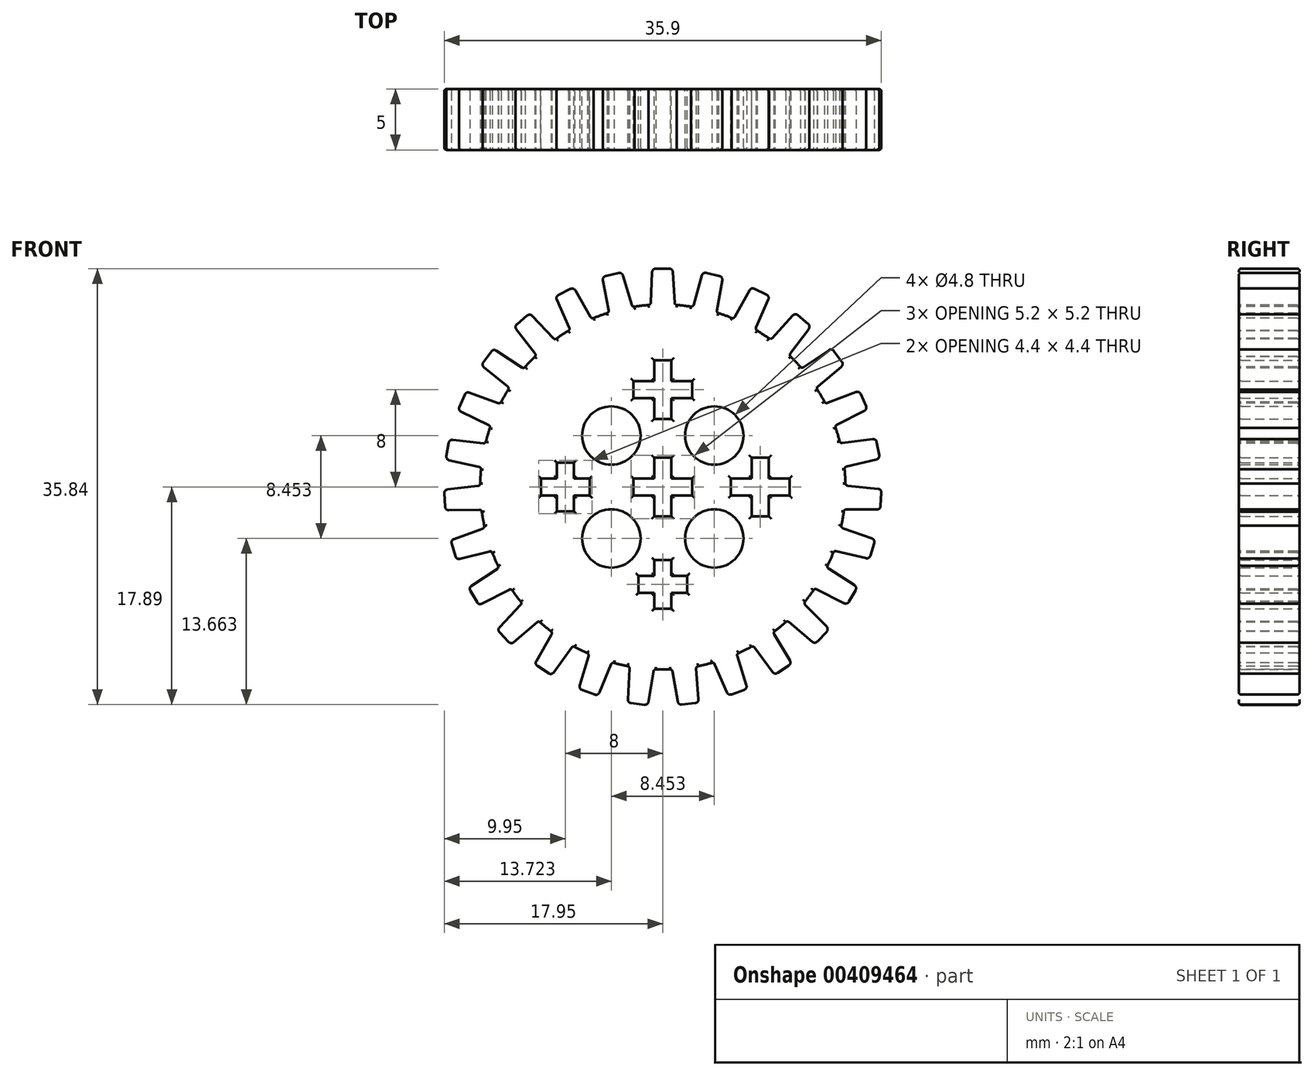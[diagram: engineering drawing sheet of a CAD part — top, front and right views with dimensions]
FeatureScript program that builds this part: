
annotation { "Feature Type Name" : "Feature", "Feature Type Description" : "" }
export const myFeature = defineFeature(function(context is Context, id is Id, definition is map)
    precondition{}
    {
        {
            var Q0;
            Q0=qCreatedBy(makeId("Front.planeOp"),FACE);
            var sketch = newSketch(context, id + "F0", { "sketchPlane" : qUnion([Q0])});
            skCircle(sketch, "E0", {"center": v(0, 0) * mm, "radius": 15 * mm});
            skLineSegment(sketch, "E1.bottom", {"start": v(0.7, -2.4) * mm, "end": v(-0.7, -2.4) * mm});
            skLineSegment(sketch, "E1.top", {"start": v(0.7, 2.4) * mm, "end": v(-0.7, 2.4) * mm});
            skLineSegment(sketch, "E1.left", {"start": v(0.7, -2.4) * mm, "end": v(0.7, 2.4) * mm});
            skLineSegment(sketch, "E1.right", {"start": v(-0.7, -2.4) * mm, "end": v(-0.7, 2.4) * mm});
            skLineSegment(sketch, "E2.bottom", {"start": v(2.4, -0.7) * mm, "end": v(-2.4, -0.7) * mm});
            skLineSegment(sketch, "E2.top", {"start": v(2.4, 0.7) * mm, "end": v(-2.4, 0.7) * mm});
            skLineSegment(sketch, "E2.left", {"start": v(2.4, -0.7) * mm, "end": v(2.4, 0.7) * mm});
            skLineSegment(sketch, "E2.right", {"start": v(-2.4, -0.7) * mm, "end": v(-2.4, 0.7) * mm});
            skLineSegment(sketch, "E3", {"start": v(-21.58, 0) * mm, "end": v(19.66, 0) * mm, "construction": true});
            skPoint(sketch, "E3.startSnap0", {"position": v(-2.4, 0) * mm});
            skPoint(sketch, "E3.endSnap0", {"position": v(-2.4, 0) * mm});
            skLineSegment(sketch, "E4", {"start": v(0, -18.97) * mm, "end": v(0, 17.04) * mm, "construction": true});
            skPoint(sketch, "E4.startSnap0", {"position": v(0, -2.4) * mm});
            skLineSegment(sketch, "E5.bottom", {"start": v(0.7, 5.6) * mm, "end": v(-0.7, 5.6) * mm});
            skLineSegment(sketch, "E5.top", {"start": v(0.7, 10.4) * mm, "end": v(-0.7, 10.4) * mm});
            skLineSegment(sketch, "E5.left", {"start": v(0.7, 5.6) * mm, "end": v(0.7, 10.4) * mm});
            skLineSegment(sketch, "E5.right", {"start": v(-0.7, 5.6) * mm, "end": v(-0.7, 10.4) * mm});
            skPoint(sketch, "E5.middle", {"position": v(0, 8) * mm});
            skLineSegment(sketch, "E6.bottom", {"start": v(2.4, 7.3) * mm, "end": v(-2.4, 7.3) * mm});
            skLineSegment(sketch, "E6.top", {"start": v(2.4, 8.7) * mm, "end": v(-2.4, 8.7) * mm});
            skLineSegment(sketch, "E6.left", {"start": v(2.4, 7.3) * mm, "end": v(2.4, 8.7) * mm});
            skLineSegment(sketch, "E6.right", {"start": v(-2.4, 7.3) * mm, "end": v(-2.4, 8.7) * mm});
            skLineSegment(sketch, "E7.bottom", {"start": v(0.7, -10) * mm, "end": v(-0.7, -10) * mm});
            skLineSegment(sketch, "E7.top", {"start": v(0.7, -6) * mm, "end": v(-0.7, -6) * mm});
            skLineSegment(sketch, "E7.left", {"start": v(0.7, -10) * mm, "end": v(0.7, -6) * mm});
            skLineSegment(sketch, "E7.right", {"start": v(-0.7, -10) * mm, "end": v(-0.7, -6) * mm});
            skPoint(sketch, "E7.middle", {"position": v(0, -8) * mm});
            skLineSegment(sketch, "E8.bottom", {"start": v(2, -8.7) * mm, "end": v(-2, -8.7) * mm});
            skLineSegment(sketch, "E8.top", {"start": v(2, -7.3) * mm, "end": v(-2, -7.3) * mm});
            skLineSegment(sketch, "E8.left", {"start": v(2, -8.7) * mm, "end": v(2, -7.3) * mm});
            skLineSegment(sketch, "E8.right", {"start": v(-2, -8.7) * mm, "end": v(-2, -7.3) * mm});
            skLineSegment(sketch, "E9.1.0", {"start": v(8.7, -2.4) * mm, "end": v(8.7, 2.4) * mm});
            skPoint(sketch, "E9.1.1", {"position": v(8, 0) * mm});
            skLineSegment(sketch, "E9.1.2", {"start": v(7.3, 2.4) * mm, "end": v(8.7, 2.4) * mm});
            skLineSegment(sketch, "E9.1.3", {"start": v(-18.97, 0) * mm, "end": v(17.04, 0) * mm, "construction": true});
            skLineSegment(sketch, "E9.1.4", {"start": v(5.6, -0.7) * mm, "end": v(10.4, -0.7) * mm});
            skLineSegment(sketch, "E9.1.5", {"start": v(5.6, 0.7) * mm, "end": v(10.4, 0.7) * mm});
            skLineSegment(sketch, "E9.1.6", {"start": v(7.3, -2.4) * mm, "end": v(7.3, 2.4) * mm});
            skLineSegment(sketch, "E9.1.7", {"start": v(7.3, -2.4) * mm, "end": v(8.7, -2.4) * mm});
            skLineSegment(sketch, "E9.1.8", {"start": v(5.6, -0.7) * mm, "end": v(5.6, 0.7) * mm});
            skPoint(sketch, "E9.1.9", {"position": v(8, 0) * mm});
            skLineSegment(sketch, "E9.1.10", {"start": v(10.4, -0.7) * mm, "end": v(10.4, 0.7) * mm});
            skLineSegment(sketch, "E9.1.11", {"start": v(-8.7, -2) * mm, "end": v(-8.7, 2) * mm});
            skLineSegment(sketch, "E9.1.12", {"start": v(-10, 0.7) * mm, "end": v(-6, 0.7) * mm});
            skLineSegment(sketch, "E9.1.13", {"start": v(-8.7, 2) * mm, "end": v(-7.3, 2) * mm});
            skLineSegment(sketch, "E9.1.14", {"start": v(-8.7, -2) * mm, "end": v(-7.3, -2) * mm});
            skPoint(sketch, "E9.1.15", {"position": v(-8, 0) * mm});
            skLineSegment(sketch, "E9.1.16", {"start": v(-10, -0.7) * mm, "end": v(-6, -0.7) * mm});
            skLineSegment(sketch, "E9.1.17", {"start": v(-7.3, -2) * mm, "end": v(-7.3, 2) * mm});
            skPoint(sketch, "E9.1.18", {"position": v(-8, 0) * mm});
            skLineSegment(sketch, "E9.1.19", {"start": v(-6, -0.7) * mm, "end": v(-6, 0.7) * mm});
            skLineSegment(sketch, "E9.1.20", {"start": v(-10, -0.7) * mm, "end": v(-10, 0.7) * mm});
            skLineSegment(sketch, "E9.anchor1", {"start": v(0, 0) * mm, "end": v(0, -18.97) * mm, "construction": true});
            skLineSegment(sketch, "E9.anchor2", {"start": v(0, 0) * mm, "end": v(-18.97, 0) * mm, "construction": true});
            skLineSegment(sketch, "E10", {"start": v(0, 0) * mm, "end": v(8.45, 8.45) * mm, "construction": true});
            skCircle(sketch, "E11", {"center": v(4.23, 4.23) * mm, "radius": 2.4 * mm});
            skCircle(sketch, "E12.1.0", {"center": v(4.23, -4.23) * mm, "radius": 2.4 * mm});
            skCircle(sketch, "E12.2.0", {"center": v(-4.23, -4.23) * mm, "radius": 2.4 * mm});
            skCircle(sketch, "E12.3.0", {"center": v(-4.23, 4.23) * mm, "radius": 2.4 * mm});
            skLineSegment(sketch, "E12.anchor1", {"start": v(0, 0) * mm, "end": v(4.23, 4.23) * mm, "construction": true});
            skLineSegment(sketch, "E12.anchor2", {"start": v(0, 0) * mm, "end": v(-4.23, 4.23) * mm, "construction": true});
            skSolve(sketch);
        }
        {
            var Q0;
            Q0=makeQuery(id+"F0.imprint","IMPRINT",FACE,{"disambiguationData":[TD([[makeQuery(id+"F0.imprint","IMPRINT",EDGE,{"derivedFrom":sQuery(id+"F0.wireOp",EDGE,"E0")}),1.0]])]});
            extrude(context, id + "F1", {"entities" : qUnion([Q0]), "depth" : 5 * mm});
        }
        {
            var Q0;
            Q0=makeQuery(id+"F1.opExtrude","CAP_FACE",FACE,{"disambiguationData":[OSD([sQuery(id+"F0.wireOp",EDGE,"E0"),sQuery(id+"F0.wireOp",EDGE,"E1.bottom"),sQuery(id+"F0.wireOp",EDGE,"E1.top"),sQuery(id+"F0.wireOp",EDGE,"E1.left"),sQuery(id+"F0.wireOp",EDGE,"E1.right"),sQuery(id+"F0.wireOp",EDGE,"E2.bottom"),sQuery(id+"F0.wireOp",EDGE,"E2.top"),sQuery(id+"F0.wireOp",EDGE,"E2.left"),sQuery(id+"F0.wireOp",EDGE,"E2.right")])],"isStart":false});
            var sketch = newSketch(context, id + "F2", { "sketchPlane" : qUnion([Q0])});
            skLineSegment(sketch, "E13.bottom", {"start": v(-0.58, 17.95) * mm, "end": v(0.52, 17.95) * mm});
            skLineSegment(sketch, "E13.left", {"start": v(-0.88, 17.66) * mm, "end": v(-1, 15.14) * mm});
            skLineSegment(sketch, "E13.right", {"start": v(0.82, 17.66) * mm, "end": v(0.97, 15.14) * mm});
            skPoint(sketch, "E14.visualSharp", {"position": v(-0.87, 17.95) * mm});
            skArc(sketch, "E14.filletArc", {"start": v(-0.58, 17.95) * mm, "mid": v(-0.79, 17.86) * mm, "end": v(-0.88, 17.66) * mm});
            skPoint(sketch, "E15.visualSharp", {"position": v(0.8, 17.95) * mm});
            skArc(sketch, "E15.filletArc", {"start": v(0.82, 17.66) * mm, "mid": v(0.73, 17.86) * mm, "end": v(0.52, 17.95) * mm});
            skLineSegment(sketch, "E16", {"start": v(0, -26.44) * mm, "end": v(0, 27.35) * mm, "construction": true});
            skPoint(sketch, "E17.visualSharp", {"position": v(-1, 14.93) * mm});
            skArc(sketch, "E17.filletArc", {"start": v(-1.17, 14.95) * mm, "mid": v(-1.05, 15.02) * mm, "end": v(-1, 15.14) * mm});
            skPoint(sketch, "E18.visualSharp", {"position": v(0.98, 14.94) * mm});
            skArc(sketch, "E18.filletArc", {"start": v(0.97, 15.14) * mm, "mid": v(1.02, 15.02) * mm, "end": v(1.15, 14.96) * mm});
            skSolve(sketch);
        }
        {
            var Q0;
            Q0=makeQuery(id+"F2.imprint","IMPRINT",FACE,{"disambiguationData":[TD([[makeQuery(id+"F2.imprint","IMPRINT",EDGE,{"derivedFrom":sQuery(id+"F2.wireOp",EDGE,"E13.bottom")}),-1.0]])]});
            var Q1;
            Q1=makeQuery(id+"F1.opExtrude","CAP_FACE",FACE,{"disambiguationData":[OSD([sQuery(id+"F0.wireOp",EDGE,"E0"),sQuery(id+"F0.wireOp",EDGE,"E1.bottom"),sQuery(id+"F0.wireOp",EDGE,"E1.top"),sQuery(id+"F0.wireOp",EDGE,"E1.left"),sQuery(id+"F0.wireOp",EDGE,"E1.right"),sQuery(id+"F0.wireOp",EDGE,"E2.bottom"),sQuery(id+"F0.wireOp",EDGE,"E2.top"),sQuery(id+"F0.wireOp",EDGE,"E2.left"),sQuery(id+"F0.wireOp",EDGE,"E2.right"),sQuery(id+"F0.wireOp",EDGE,"E5.bottom"),sQuery(id+"F0.wireOp",EDGE,"E5.top"),sQuery(id+"F0.wireOp",EDGE,"E5.left"),sQuery(id+"F0.wireOp",EDGE,"E5.right"),sQuery(id+"F0.wireOp",EDGE,"E6.bottom"),sQuery(id+"F0.wireOp",EDGE,"E6.top"),sQuery(id+"F0.wireOp",EDGE,"E6.left"),sQuery(id+"F0.wireOp",EDGE,"E6.right"),sQuery(id+"F0.wireOp",EDGE,"E7.bottom"),sQuery(id+"F0.wireOp",EDGE,"E7.top"),sQuery(id+"F0.wireOp",EDGE,"E7.left"),sQuery(id+"F0.wireOp",EDGE,"E7.right"),sQuery(id+"F0.wireOp",EDGE,"E8.bottom"),sQuery(id+"F0.wireOp",EDGE,"E8.top"),sQuery(id+"F0.wireOp",EDGE,"E8.left"),sQuery(id+"F0.wireOp",EDGE,"E8.right"),sQuery(id+"F0.wireOp",EDGE,"E9.1.0"),sQuery(id+"F0.wireOp",EDGE,"E9.1.2"),sQuery(id+"F0.wireOp",EDGE,"E9.1.4"),sQuery(id+"F0.wireOp",EDGE,"E9.1.5"),sQuery(id+"F0.wireOp",EDGE,"E9.1.6"),sQuery(id+"F0.wireOp",EDGE,"E9.1.7"),sQuery(id+"F0.wireOp",EDGE,"E9.1.8"),sQuery(id+"F0.wireOp",EDGE,"E9.1.10"),sQuery(id+"F0.wireOp",EDGE,"E9.1.11"),sQuery(id+"F0.wireOp",EDGE,"E9.1.12"),sQuery(id+"F0.wireOp",EDGE,"E9.1.13"),sQuery(id+"F0.wireOp",EDGE,"E9.1.14"),sQuery(id+"F0.wireOp",EDGE,"E9.1.16"),sQuery(id+"F0.wireOp",EDGE,"E9.1.17"),sQuery(id+"F0.wireOp",EDGE,"E9.1.19"),sQuery(id+"F0.wireOp",EDGE,"E9.1.20"),sQuery(id+"F0.wireOp",EDGE,"E11"),sQuery(id+"F0.wireOp",EDGE,"E12.1.0"),sQuery(id+"F0.wireOp",EDGE,"E12.2.0"),sQuery(id+"F0.wireOp",EDGE,"E12.3.0")])],"isStart":true});
            extrude(context, id + "F3", {"entities" : qUnion([Q0]), "flatOperationType" : FlatOperationType.REMOVE, "endBound" : BoundingType.UP_TO_SURFACE, "oppositeDirection" : true, "endBoundEntityFace" : qUnion([Q1]), "offsetDistance" : 25 * mm, "depth" : 25 * mm, "domain" : OperationDomain.MODEL});
        }
        {
            var Q0;
            Q0=makeQuery(id+"F3.opExtrude","SWEPT_BODY",BODY,{"disambiguationData":[OSD([sQuery(id+"F0.wireOp",EDGE,"E0"),sQuery(id+"F2.wireOp",EDGE,"E13.bottom"),sQuery(id+"F2.wireOp",EDGE,"E13.left"),sQuery(id+"F2.wireOp",EDGE,"E13.right"),sQuery(id+"F2.wireOp",EDGE,"E14.filletArc"),sQuery(id+"F2.wireOp",EDGE,"E15.filletArc")])]});
            var Q1;
            Q1=makeQuery(id+"F1.opExtrude","CAP_EDGE",EDGE,{"disambiguationData":[OSD([sQuery(id+"F0.wireOp",EDGE,"E0")])],"isStart":false});
            circularPattern(context, id + "F4", {"operationType" : NewBodyOperationType.ADD, "entities" : qUnion([Q0]), "axis" : qUnion([Q1]), "angle" : 360 * degree, "instanceCount" : 27, "equalSpace" : true});
        }
        {
            var Q0;
            {var subQ0=sQuery(id+"F0.wireOp",EDGE,"E0");var subQ1=makeQuery(id+"F3.opExtrude","CAP_FACE",FACE,{"disambiguationData":[OSD([subQ0,sQuery(id+"F2.wireOp",EDGE,"E13.bottom"),sQuery(id+"F2.wireOp",EDGE,"E13.left"),sQuery(id+"F2.wireOp",EDGE,"E13.right"),sQuery(id+"F2.wireOp",EDGE,"E14.filletArc"),sQuery(id+"F2.wireOp",EDGE,"E15.filletArc")])],"isStart":true});Q0=makeQuery(id+"F4.boolean.opBoolean","MERGE",FACE,{"derivedFrom":[makeQuery(id+"F1.opExtrude","CAP_FACE",FACE,{"disambiguationData":[OSD([subQ0,sQuery(id+"F0.wireOp",EDGE,"E1.bottom"),sQuery(id+"F0.wireOp",EDGE,"E1.top"),sQuery(id+"F0.wireOp",EDGE,"E1.left"),sQuery(id+"F0.wireOp",EDGE,"E1.right"),sQuery(id+"F0.wireOp",EDGE,"E2.bottom"),sQuery(id+"F0.wireOp",EDGE,"E2.top"),sQuery(id+"F0.wireOp",EDGE,"E2.left"),sQuery(id+"F0.wireOp",EDGE,"E2.right"),sQuery(id+"F0.wireOp",EDGE,"E5.bottom"),sQuery(id+"F0.wireOp",EDGE,"E5.top"),sQuery(id+"F0.wireOp",EDGE,"E5.left"),sQuery(id+"F0.wireOp",EDGE,"E5.right"),sQuery(id+"F0.wireOp",EDGE,"E6.bottom"),sQuery(id+"F0.wireOp",EDGE,"E6.top"),sQuery(id+"F0.wireOp",EDGE,"E6.left"),sQuery(id+"F0.wireOp",EDGE,"E6.right"),sQuery(id+"F0.wireOp",EDGE,"E7.bottom"),sQuery(id+"F0.wireOp",EDGE,"E7.top"),sQuery(id+"F0.wireOp",EDGE,"E7.left"),sQuery(id+"F0.wireOp",EDGE,"E7.right"),sQuery(id+"F0.wireOp",EDGE,"E8.bottom"),sQuery(id+"F0.wireOp",EDGE,"E8.top"),sQuery(id+"F0.wireOp",EDGE,"E8.left"),sQuery(id+"F0.wireOp",EDGE,"E8.right"),sQuery(id+"F0.wireOp",EDGE,"E9.1.0"),sQuery(id+"F0.wireOp",EDGE,"E9.1.2"),sQuery(id+"F0.wireOp",EDGE,"E9.1.4"),sQuery(id+"F0.wireOp",EDGE,"E9.1.5"),sQuery(id+"F0.wireOp",EDGE,"E9.1.6"),sQuery(id+"F0.wireOp",EDGE,"E9.1.7"),sQuery(id+"F0.wireOp",EDGE,"E9.1.8"),sQuery(id+"F0.wireOp",EDGE,"E9.1.10"),sQuery(id+"F0.wireOp",EDGE,"E9.1.11"),sQuery(id+"F0.wireOp",EDGE,"E9.1.12"),sQuery(id+"F0.wireOp",EDGE,"E9.1.13"),sQuery(id+"F0.wireOp",EDGE,"E9.1.14"),sQuery(id+"F0.wireOp",EDGE,"E9.1.16"),sQuery(id+"F0.wireOp",EDGE,"E9.1.17"),sQuery(id+"F0.wireOp",EDGE,"E9.1.19"),sQuery(id+"F0.wireOp",EDGE,"E9.1.20"),sQuery(id+"F0.wireOp",EDGE,"E11"),sQuery(id+"F0.wireOp",EDGE,"E12.1.0"),sQuery(id+"F0.wireOp",EDGE,"E12.2.0"),sQuery(id+"F0.wireOp",EDGE,"E12.3.0")])],"isStart":false}),subQ1,makeQuery(id+"F4.opPattern","COPY",FACE,{"derivedFrom":subQ1,"instanceName":"1"}),makeQuery(id+"F4.opPattern","COPY",FACE,{"derivedFrom":subQ1,"instanceName":"2"}),makeQuery(id+"F4.opPattern","COPY",FACE,{"derivedFrom":subQ1,"instanceName":"3"}),makeQuery(id+"F4.opPattern","COPY",FACE,{"derivedFrom":subQ1,"instanceName":"4"}),makeQuery(id+"F4.opPattern","COPY",FACE,{"derivedFrom":subQ1,"instanceName":"5"}),makeQuery(id+"F4.opPattern","COPY",FACE,{"derivedFrom":subQ1,"instanceName":"6"}),makeQuery(id+"F4.opPattern","COPY",FACE,{"derivedFrom":subQ1,"instanceName":"7"}),makeQuery(id+"F4.opPattern","COPY",FACE,{"derivedFrom":subQ1,"instanceName":"8"}),makeQuery(id+"F4.opPattern","COPY",FACE,{"derivedFrom":subQ1,"instanceName":"9"}),makeQuery(id+"F4.opPattern","COPY",FACE,{"derivedFrom":subQ1,"instanceName":"10"}),makeQuery(id+"F4.opPattern","COPY",FACE,{"derivedFrom":subQ1,"instanceName":"11"}),makeQuery(id+"F4.opPattern","COPY",FACE,{"derivedFrom":subQ1,"instanceName":"12"}),makeQuery(id+"F4.opPattern","COPY",FACE,{"derivedFrom":subQ1,"instanceName":"13"}),makeQuery(id+"F4.opPattern","COPY",FACE,{"derivedFrom":subQ1,"instanceName":"14"}),makeQuery(id+"F4.opPattern","COPY",FACE,{"derivedFrom":subQ1,"instanceName":"15"}),makeQuery(id+"F4.opPattern","COPY",FACE,{"derivedFrom":subQ1,"instanceName":"16"}),makeQuery(id+"F4.opPattern","COPY",FACE,{"derivedFrom":subQ1,"instanceName":"17"}),makeQuery(id+"F4.opPattern","COPY",FACE,{"derivedFrom":subQ1,"instanceName":"18"}),makeQuery(id+"F4.opPattern","COPY",FACE,{"derivedFrom":subQ1,"instanceName":"19"}),makeQuery(id+"F4.opPattern","COPY",FACE,{"derivedFrom":subQ1,"instanceName":"20"}),makeQuery(id+"F4.opPattern","COPY",FACE,{"derivedFrom":subQ1,"instanceName":"21"}),makeQuery(id+"F4.opPattern","COPY",FACE,{"derivedFrom":subQ1,"instanceName":"22"}),makeQuery(id+"F4.opPattern","COPY",FACE,{"derivedFrom":subQ1,"instanceName":"23"}),makeQuery(id+"F4.opPattern","COPY",FACE,{"derivedFrom":subQ1,"instanceName":"24"}),makeQuery(id+"F4.opPattern","COPY",FACE,{"derivedFrom":subQ1,"instanceName":"25"}),makeQuery(id+"F4.opPattern","COPY",FACE,{"derivedFrom":subQ1,"instanceName":"26"})]});}
            var Q1;
            {var subQ0=sQuery(id+"F0.wireOp",EDGE,"E12.3.0");var subQ1=sQuery(id+"F0.wireOp",EDGE,"E12.2.0");var subQ2=sQuery(id+"F0.wireOp",EDGE,"E12.1.0");var subQ3=sQuery(id+"F0.wireOp",EDGE,"E11");var subQ4=sQuery(id+"F0.wireOp",EDGE,"E9.1.20");var subQ5=sQuery(id+"F0.wireOp",EDGE,"E9.1.19");var subQ6=sQuery(id+"F0.wireOp",EDGE,"E9.1.17");var subQ7=sQuery(id+"F0.wireOp",EDGE,"E9.1.16");var subQ8=sQuery(id+"F0.wireOp",EDGE,"E9.1.14");var subQ9=sQuery(id+"F0.wireOp",EDGE,"E9.1.13");var subQ10=sQuery(id+"F0.wireOp",EDGE,"E9.1.12");var subQ11=sQuery(id+"F0.wireOp",EDGE,"E9.1.11");var subQ12=sQuery(id+"F0.wireOp",EDGE,"E9.1.10");var subQ13=sQuery(id+"F0.wireOp",EDGE,"E9.1.8");var subQ14=sQuery(id+"F0.wireOp",EDGE,"E9.1.7");var subQ15=sQuery(id+"F0.wireOp",EDGE,"E9.1.6");var subQ16=sQuery(id+"F0.wireOp",EDGE,"E9.1.5");var subQ17=sQuery(id+"F0.wireOp",EDGE,"E9.1.4");var subQ18=sQuery(id+"F0.wireOp",EDGE,"E9.1.2");var subQ19=sQuery(id+"F0.wireOp",EDGE,"E9.1.0");var subQ20=sQuery(id+"F0.wireOp",EDGE,"E8.right");var subQ21=sQuery(id+"F0.wireOp",EDGE,"E8.left");var subQ22=sQuery(id+"F0.wireOp",EDGE,"E8.top");var subQ23=sQuery(id+"F0.wireOp",EDGE,"E8.bottom");var subQ24=sQuery(id+"F0.wireOp",EDGE,"E7.right");var subQ25=sQuery(id+"F0.wireOp",EDGE,"E7.left");var subQ26=sQuery(id+"F0.wireOp",EDGE,"E7.top");var subQ27=sQuery(id+"F0.wireOp",EDGE,"E7.bottom");var subQ28=sQuery(id+"F0.wireOp",EDGE,"E6.right");var subQ29=sQuery(id+"F0.wireOp",EDGE,"E6.left");var subQ30=sQuery(id+"F0.wireOp",EDGE,"E6.top");var subQ31=sQuery(id+"F0.wireOp",EDGE,"E6.bottom");var subQ32=sQuery(id+"F0.wireOp",EDGE,"E5.right");var subQ33=sQuery(id+"F0.wireOp",EDGE,"E5.left");var subQ34=sQuery(id+"F0.wireOp",EDGE,"E5.top");var subQ35=sQuery(id+"F0.wireOp",EDGE,"E5.bottom");var subQ36=sQuery(id+"F0.wireOp",EDGE,"E2.right");var subQ37=sQuery(id+"F0.wireOp",EDGE,"E2.left");var subQ38=sQuery(id+"F0.wireOp",EDGE,"E2.top");var subQ39=sQuery(id+"F0.wireOp",EDGE,"E2.bottom");var subQ40=sQuery(id+"F0.wireOp",EDGE,"E1.right");var subQ41=sQuery(id+"F0.wireOp",EDGE,"E1.left");var subQ42=sQuery(id+"F0.wireOp",EDGE,"E1.top");var subQ43=sQuery(id+"F0.wireOp",EDGE,"E1.bottom");var subQ44=sQuery(id+"F0.wireOp",EDGE,"E0");var subQ45=makeQuery(id+"F3.opExtrude","CAP_FACE",FACE,{"disambiguationData":[OSD([subQ44,subQ43,subQ42,subQ41,subQ40,subQ39,subQ38,subQ37,subQ36,subQ35,subQ34,subQ33,subQ32,subQ31,subQ30,subQ29,subQ28,subQ27,subQ26,subQ25,subQ24,subQ23,subQ22,subQ21,subQ20,subQ19,subQ18,subQ17,subQ16,subQ15,subQ14,subQ13,subQ12,subQ11,subQ10,subQ9,subQ8,subQ7,subQ6,subQ5,subQ4,subQ3,subQ2,subQ1,subQ0])],"isStart":false});Q1=makeQuery(id+"F4.boolean.opBoolean","MERGE",FACE,{"derivedFrom":[makeQuery(id+"F1.opExtrude","CAP_FACE",FACE,{"disambiguationData":[OSD([subQ44,subQ43,subQ42,subQ41,subQ40,subQ39,subQ38,subQ37,subQ36,subQ35,subQ34,subQ33,subQ32,subQ31,subQ30,subQ29,subQ28,subQ27,subQ26,subQ25,subQ24,subQ23,subQ22,subQ21,subQ20,subQ19,subQ18,subQ17,subQ16,subQ15,subQ14,subQ13,subQ12,subQ11,subQ10,subQ9,subQ8,subQ7,subQ6,subQ5,subQ4,subQ3,subQ2,subQ1,subQ0])],"isStart":true}),subQ45,makeQuery(id+"F4.opPattern","COPY",FACE,{"derivedFrom":subQ45,"instanceName":"1"}),makeQuery(id+"F4.opPattern","COPY",FACE,{"derivedFrom":subQ45,"instanceName":"2"}),makeQuery(id+"F4.opPattern","COPY",FACE,{"derivedFrom":subQ45,"instanceName":"3"}),makeQuery(id+"F4.opPattern","COPY",FACE,{"derivedFrom":subQ45,"instanceName":"4"}),makeQuery(id+"F4.opPattern","COPY",FACE,{"derivedFrom":subQ45,"instanceName":"5"}),makeQuery(id+"F4.opPattern","COPY",FACE,{"derivedFrom":subQ45,"instanceName":"6"}),makeQuery(id+"F4.opPattern","COPY",FACE,{"derivedFrom":subQ45,"instanceName":"7"}),makeQuery(id+"F4.opPattern","COPY",FACE,{"derivedFrom":subQ45,"instanceName":"8"}),makeQuery(id+"F4.opPattern","COPY",FACE,{"derivedFrom":subQ45,"instanceName":"9"}),makeQuery(id+"F4.opPattern","COPY",FACE,{"derivedFrom":subQ45,"instanceName":"10"}),makeQuery(id+"F4.opPattern","COPY",FACE,{"derivedFrom":subQ45,"instanceName":"11"}),makeQuery(id+"F4.opPattern","COPY",FACE,{"derivedFrom":subQ45,"instanceName":"12"}),makeQuery(id+"F4.opPattern","COPY",FACE,{"derivedFrom":subQ45,"instanceName":"13"}),makeQuery(id+"F4.opPattern","COPY",FACE,{"derivedFrom":subQ45,"instanceName":"14"}),makeQuery(id+"F4.opPattern","COPY",FACE,{"derivedFrom":subQ45,"instanceName":"15"}),makeQuery(id+"F4.opPattern","COPY",FACE,{"derivedFrom":subQ45,"instanceName":"16"}),makeQuery(id+"F4.opPattern","COPY",FACE,{"derivedFrom":subQ45,"instanceName":"17"}),makeQuery(id+"F4.opPattern","COPY",FACE,{"derivedFrom":subQ45,"instanceName":"18"}),makeQuery(id+"F4.opPattern","COPY",FACE,{"derivedFrom":subQ45,"instanceName":"19"}),makeQuery(id+"F4.opPattern","COPY",FACE,{"derivedFrom":subQ45,"instanceName":"20"}),makeQuery(id+"F4.opPattern","COPY",FACE,{"derivedFrom":subQ45,"instanceName":"21"}),makeQuery(id+"F4.opPattern","COPY",FACE,{"derivedFrom":subQ45,"instanceName":"22"}),makeQuery(id+"F4.opPattern","COPY",FACE,{"derivedFrom":subQ45,"instanceName":"23"}),makeQuery(id+"F4.opPattern","COPY",FACE,{"derivedFrom":subQ45,"instanceName":"24"}),makeQuery(id+"F4.opPattern","COPY",FACE,{"derivedFrom":subQ45,"instanceName":"25"}),makeQuery(id+"F4.opPattern","COPY",FACE,{"derivedFrom":subQ45,"instanceName":"26"})]});}
            fillet(context, id + "F5", {"entities" : qUnion([Q0, Q1]), "radius" : .2 * mm, "tangentPropagation" : true, "allowEdgeOverflow" : false});
        }
    });
